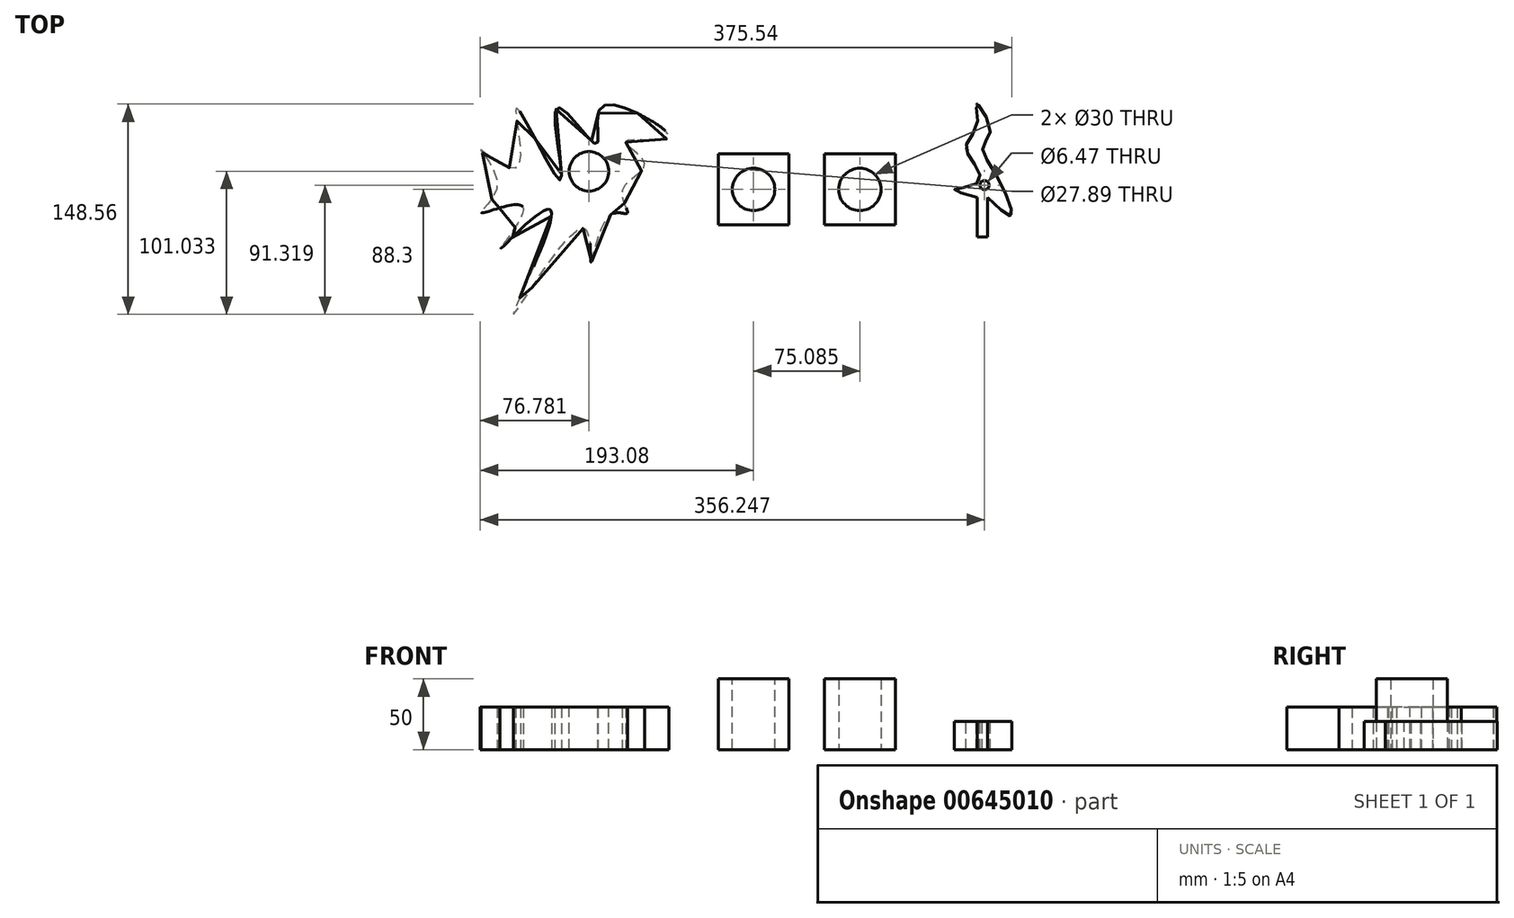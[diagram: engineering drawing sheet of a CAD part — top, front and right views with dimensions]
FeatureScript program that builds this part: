
annotation { "Feature Type Name" : "Feature", "Feature Type Description" : "" }
export const myFeature = defineFeature(function(context is Context, id is Id, definition is map)
    precondition{}
    {
        {
            var Q0;
            Q0=qCreatedBy(makeId("Top.planeOp"),FACE);
            var sketch = newSketch(context, id + "F0", { "sketchPlane" : qUnion([Q0])});
            skLineSegment(sketch, "E0.bottom", {"start": v(-25, -25) * mm, "end": v(25, -25) * mm});
            skLineSegment(sketch, "E0.top", {"start": v(-25, 25) * mm, "end": v(25, 25) * mm});
            skLineSegment(sketch, "E0.left", {"start": v(-25, -25) * mm, "end": v(-25, 25) * mm});
            skLineSegment(sketch, "E0.right", {"start": v(25, -25) * mm, "end": v(25, 25) * mm});
            skPoint(sketch, "E0.middle", {"position": v(0, 0) * mm});
            skSolve(sketch);
        }
        {
            var Q0;
            Q0 = qSketchRegion(id + "F0", true);
            extrude(context, id + "F1", {"entities" : qUnion([Q0]), "depth" : 50 * mm, "offsetDistance" : 25.4 * mm});
        }
        {
            var Q0;
            Q0=makeQuery(id+"F1.opExtrude","CAP_FACE",FACE,{"disambiguationData":[OSD([sQuery(id+"F0.wireOp",EDGE,"E0.bottom"),sQuery(id+"F0.wireOp",EDGE,"E0.top"),sQuery(id+"F0.wireOp",EDGE,"E0.left"),sQuery(id+"F0.wireOp",EDGE,"E0.right")])],"isStart":false});
            var sketch = newSketch(context, id + "F2", { "sketchPlane" : qUnion([Q0])});
            skCircle(sketch, "E1", {"center": v(0, 0) * mm, "radius": 15 * mm});
            skSolve(sketch);
        }
        {
            var Q0;
            Q0 = qSketchRegion(id + "F2", true);
            extrude(context, id + "F3", {"entities" : qUnion([Q0]), "operationType" : NewBodyOperationType.REMOVE, "oppositeDirection" : true, "depth" : 50 * mm, "offsetDistance" : 25 * mm});
        }
        {
            var Q0;
            Q0=qCreatedBy(makeId("Top.planeOp"),FACE);
            var sketch = newSketch(context, id + "F4", { "sketchPlane" : qUnion([Q0])});
            skLineSegment(sketch, "E2.bottom", {"start": v(100.09, -25) * mm, "end": v(50.09, -25) * mm});
            skLineSegment(sketch, "E2.top", {"start": v(100.09, 25) * mm, "end": v(50.09, 25) * mm});
            skLineSegment(sketch, "E2.left", {"start": v(100.09, -25) * mm, "end": v(100.09, 25) * mm});
            skLineSegment(sketch, "E2.right", {"start": v(50.09, -25) * mm, "end": v(50.09, 25) * mm});
            skPoint(sketch, "E2.middle", {"position": v(75.09, 0) * mm});
            skCircle(sketch, "E3", {"center": v(75.09, 0) * mm, "radius": 15 * mm});
            skSolve(sketch);
        }
        {
            var Q0;
            Q0 = qSketchRegion(id + "F4", true);
            extrude(context, id + "F5", {"entities" : qUnion([Q0]), "depth" : 50 * mm, "offsetDistance" : 25 * mm});
        }
        {
            var Q0;
            Q0=qCreatedBy(makeId("Top.planeOp"),FACE);
            var sketch = newSketch(context, id + "F6", { "sketchPlane" : qUnion([Q0])});
            skFitSpline(sketch, "E4", {"points": [v(-81.77, 53.64) * mm, v(-109.33, 55.37) * mm, v(-111.37, 32.07) * mm, v(-138.75, 57.58) * mm, v(-136.54, 6.62) * mm, v(-167.42, 57.5) * mm, v(-167.28, 15.6) * mm, v(-192.95, 27.96) * mm, v(-181.12, 3.15) * mm, v(-192.09, -16.54) * mm, v(-163.05, -12.37) * mm, v(-179.04, -42.1) * mm, v(-143.8, -14.34) * mm, v(-169.72, -88.27) * mm, v(-120.43, -27.45) * mm, v(-114.89, -51.4) * mm, v(-101.47, -18.29) * mm, v(-89.23, -16.8) * mm, v(-92.4, 0) * mm, v(-76.94, 18) * mm, v(-90.18, 34.05) * mm, v(-60.7, 35.97) * mm, v(-81.77, 53.64) * mm]});
            skSolve(sketch);
        }
        {
            var Q0;
            Q0 = qSketchRegion(id + "F6", true);
            extrude(context, id + "F7", {"entities" : qUnion([Q0]), "depth" : 30 * mm, "offsetDistance" : 25 * mm});
        }
        {
            var Q0;
            Q0=makeQuery(id+"F7.opExtrude","CAP_FACE",FACE,{"disambiguationData":[OSD([sQuery(id+"F6.wireOp",EDGE,"E4")])],"isStart":false});
            var sketch = newSketch(context, id + "F8", { "sketchPlane" : qUnion([Q0])});
            skCircle(sketch, "E5", {"center": v(-116.3, 12.73) * mm, "radius": 13.94 * mm});
            skSolve(sketch);
        }
        {
            var Q0;
            Q0 = qSketchRegion(id + "F8", true);
            extrude(context, id + "F9", {"entities" : qUnion([Q0]), "operationType" : NewBodyOperationType.REMOVE, "oppositeDirection" : true, "depth" : 30 * mm, "offsetDistance" : 25 * mm});
        }
        {
            var Q0;
            Q0=qCreatedBy(makeId("Top.planeOp"),FACE);
            var sketch = newSketch(context, id + "F10", { "sketchPlane" : qUnion([Q0])});
            skLineSegment(sketch, "E6.bottom", {"start": v(157.85, -5.54) * mm, "end": v(165.27, -5.54) * mm});
            skLineSegment(sketch, "E6.top", {"start": v(157.85, -33.73) * mm, "end": v(165.27, -33.73) * mm});
            skLineSegment(sketch, "E6.left", {"start": v(157.85, -5.54) * mm, "end": v(157.85, -33.73) * mm});
            skLineSegment(sketch, "E6.right", {"start": v(165.27, -5.54) * mm, "end": v(165.27, -33.73) * mm});
            skFitSpline(sketch, "E7", {"points": [v(157.85, -5.54) * mm, v(142.02, 0) * mm, v(157.85, 4.36) * mm, v(157.85, 15.24) * mm, v(149.93, 29.59) * mm, v(157.85, 45.91) * mm, v(157.85, 60.26) * mm, v(167.25, 41.46) * mm, v(161.8, 30.58) * mm, v(171.2, 10.3) * mm, v(182.09, -18.4) * mm, v(165.27, -5.54) * mm], "startDerivative": vector(-289.1, 74.2) * mm, "endDerivative": vector(-229.57, 222.26) * mm});
            skSolve(sketch);
        }
        {
            var Q0;
            Q0 = qSketchRegion(id + "F10", true);
            extrude(context, id + "F11", {"entities" : qUnion([Q0]), "depth" : 20 * mm, "offsetDistance" : 25 * mm});
        }
        {
            var Q0;
            Q0=makeQuery(id+"F11.opExtrude","CAP_FACE",FACE,{"disambiguationData":[OSD([sQuery(id+"F10.wireOp",EDGE,"E6.top"),sQuery(id+"F10.wireOp",EDGE,"E6.left"),sQuery(id+"F10.wireOp",EDGE,"E6.right"),sQuery(id+"F10.wireOp",EDGE,"E7")])],"isStart":false});
            var sketch = newSketch(context, id + "F12", { "sketchPlane" : qUnion([Q0])});
            skCircle(sketch, "E8", {"center": v(163.17, 3.02) * mm, "radius": 3.24 * mm});
            skSolve(sketch);
        }
        {
            var Q0;
            Q0=makeQuery(id+"F12.imprint","IMPRINT",FACE,{"disambiguationData":[TD([[makeQuery(id+"F12.imprint","IMPRINT",EDGE,{"derivedFrom":sQuery(id+"F12.wireOp",EDGE,"E8")}),1.0]])]});
            extrude(context, id + "F13", {"entities" : qUnion([Q0]), "operationType" : NewBodyOperationType.REMOVE, "oppositeDirection" : true, "depth" : 20 * mm, "offsetDistance" : 25 * mm});
        }
    });
